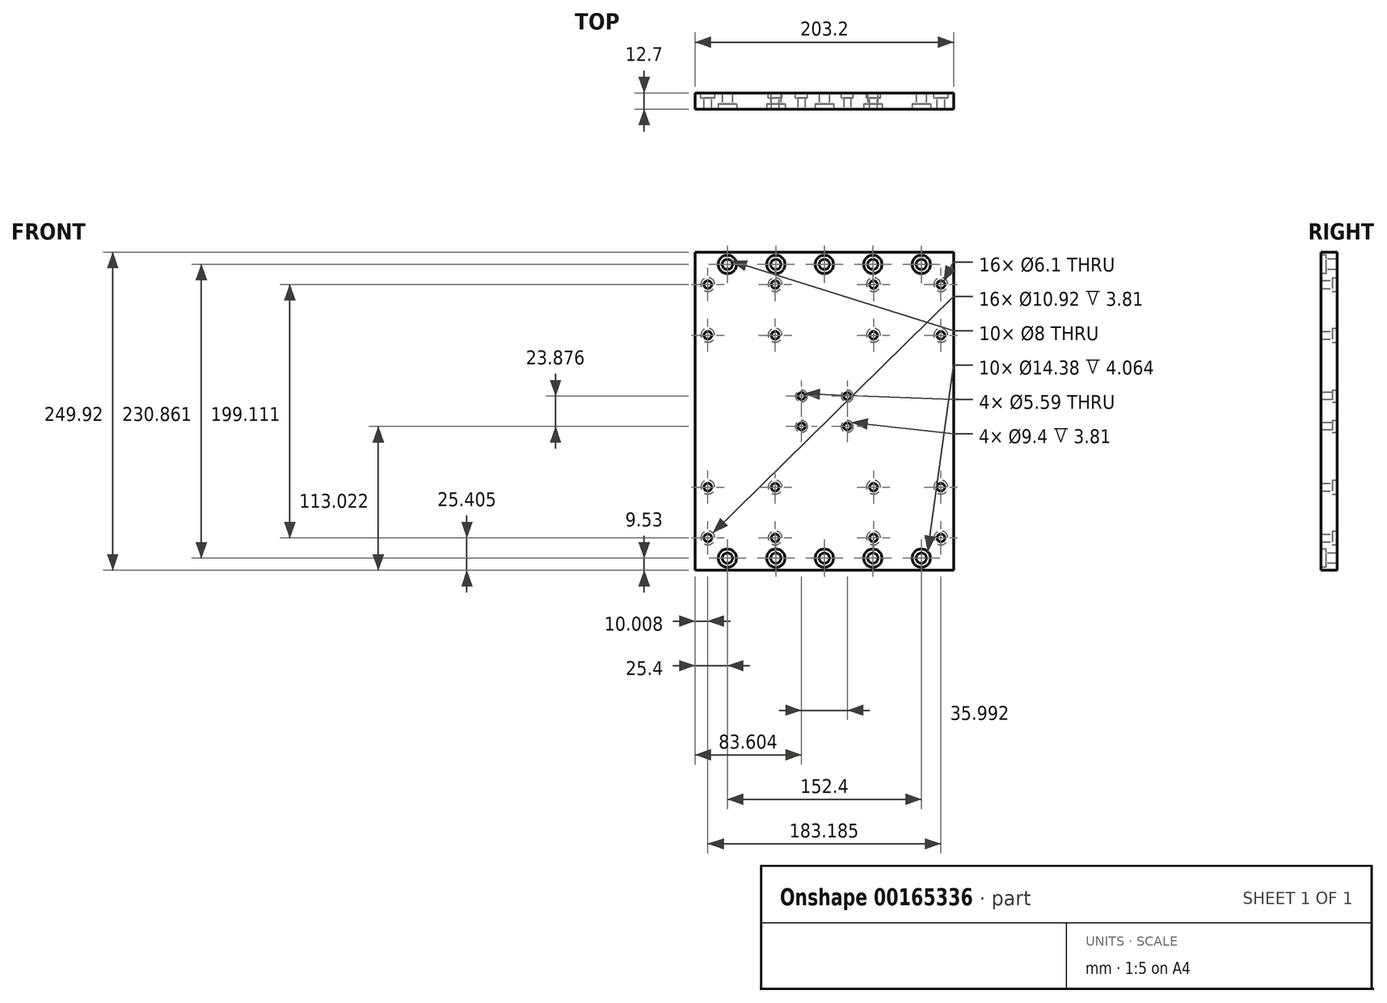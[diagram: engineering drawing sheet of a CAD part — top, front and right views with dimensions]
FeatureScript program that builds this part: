
annotation { "Feature Type Name" : "Feature", "Feature Type Description" : "" }
export const myFeature = defineFeature(function(context is Context, id is Id, definition is map)
    precondition{}
    {
        {
            var Q0;
            Q0=qCreatedBy(makeId("Front.planeOp"),FACE);
            var sketch = newSketch(context, id + "F0", { "sketchPlane" : qUnion([Q0])});
            skLineSegment(sketch, "E0.rect.bottom", {"start": v(101.6, 124.96) * mm, "end": v(-101.6, 124.96) * mm});
            skLineSegment(sketch, "E0.rect.top", {"start": v(101.6, -124.96) * mm, "end": v(-101.6, -124.96) * mm});
            skLineSegment(sketch, "E0.rect.left", {"start": v(101.6, 124.96) * mm, "end": v(101.6, -124.96) * mm});
            skLineSegment(sketch, "E0.rect.right", {"start": v(-101.6, 124.96) * mm, "end": v(-101.6, -124.96) * mm});
            skPoint(sketch, "E0.rect.middle", {"position": v(0, 0) * mm});
            skLineSegment(sketch, "E1", {"start": v(-101.6, 99.56) * mm, "end": v(101.6, 99.56) * mm, "construction": true});
            skLineSegment(sketch, "E2", {"start": v(-91.6, 124.96) * mm, "end": v(-91.6, -124.96) * mm, "construction": true});
            skLineSegment(sketch, "E3", {"start": v(-38.63, 124.96) * mm, "end": v(-38.63, -124.96) * mm, "construction": true});
            skLineSegment(sketch, "E4", {"start": v(38.63, 124.96) * mm, "end": v(38.63, -124.96) * mm, "construction": true});
            skLineSegment(sketch, "E5", {"start": v(91.6, 124.96) * mm, "end": v(91.6, -124.96) * mm, "construction": true});
            skLineSegment(sketch, "E6", {"start": v(-101.6, 59.68) * mm, "end": v(101.6, 59.68) * mm, "construction": true});
            skLineSegment(sketch, "E7", {"start": v(-101.6, -99.56) * mm, "end": v(101.6, -99.56) * mm, "construction": true});
            skLineSegment(sketch, "E8", {"start": v(-101.6, -59.68) * mm, "end": v(101.6, -59.68) * mm, "construction": true});
            skCircle(sketch, "E9", {"center": v(-91.6, 99.56) * mm, "radius": 3.05 * mm});
            skCircle(sketch, "E10", {"center": v(-38.63, 99.56) * mm, "radius": 3.05 * mm});
            skCircle(sketch, "E11", {"center": v(38.63, 99.56) * mm, "radius": 3.05 * mm});
            skCircle(sketch, "E12", {"center": v(91.6, 99.56) * mm, "radius": 3.05 * mm});
            skCircle(sketch, "E13", {"center": v(91.6, 59.68) * mm, "radius": 3.05 * mm});
            skCircle(sketch, "E14", {"center": v(-38.63, 59.68) * mm, "radius": 3.05 * mm});
            skCircle(sketch, "E15", {"center": v(38.63, 59.68) * mm, "radius": 3.05 * mm});
            skCircle(sketch, "E16", {"center": v(38.63, -59.68) * mm, "radius": 3.05 * mm});
            skCircle(sketch, "E17", {"center": v(91.6, -59.68) * mm, "radius": 3.05 * mm});
            skCircle(sketch, "E18", {"center": v(91.6, -99.56) * mm, "radius": 3.05 * mm});
            skCircle(sketch, "E19", {"center": v(38.63, -99.56) * mm, "radius": 3.05 * mm});
            skCircle(sketch, "E20", {"center": v(-38.63, -99.56) * mm, "radius": 3.05 * mm});
            skCircle(sketch, "E21", {"center": v(-38.63, -59.68) * mm, "radius": 3.05 * mm});
            skCircle(sketch, "E22", {"center": v(-91.6, -59.68) * mm, "radius": 3.05 * mm});
            skCircle(sketch, "E23", {"center": v(-91.6, -99.56) * mm, "radius": 3.05 * mm});
            skCircle(sketch, "E24", {"center": v(-91.6, 59.68) * mm, "radius": 3.05 * mm});
            skSolve(sketch);
        }
        {
            var Q0;
            Q0=qSketchRegion(id+"F0",true);
            extrude(context, id + "F1", {"entities" : qUnion([Q0]), "depth" : 12.7 * mm});
        }
        {
            var Q0;
            Q0=makeQuery(id+"F1.opExtrude","CAP_FACE",FACE,{"disambiguationData":[OSD([sQuery(id+"F0.wireOp",EDGE,"E0.rect.bottom"),sQuery(id+"F0.wireOp",EDGE,"E0.rect.top"),sQuery(id+"F0.wireOp",EDGE,"E0.rect.left"),sQuery(id+"F0.wireOp",EDGE,"E0.rect.right"),sQuery(id+"F0.wireOp",EDGE,"E9"),sQuery(id+"F0.wireOp",EDGE,"E10"),sQuery(id+"F0.wireOp",EDGE,"E11"),sQuery(id+"F0.wireOp",EDGE,"E12"),sQuery(id+"F0.wireOp",EDGE,"E13"),sQuery(id+"F0.wireOp",EDGE,"E14"),sQuery(id+"F0.wireOp",EDGE,"E15"),sQuery(id+"F0.wireOp",EDGE,"E16"),sQuery(id+"F0.wireOp",EDGE,"E17"),sQuery(id+"F0.wireOp",EDGE,"E18"),sQuery(id+"F0.wireOp",EDGE,"E19"),sQuery(id+"F0.wireOp",EDGE,"E20"),sQuery(id+"F0.wireOp",EDGE,"E21"),sQuery(id+"F0.wireOp",EDGE,"E22"),sQuery(id+"F0.wireOp",EDGE,"E23"),sQuery(id+"F0.wireOp",EDGE,"E24")])],"isStart":false});
            var sketch = newSketch(context, id + "F2", { "sketchPlane" : qUnion([Q0])});
            skPoint(sketch, "E25.rect.middle", {"position": v(0, 0) * mm});
            skLineSegment(sketch, "E26.rect.bottom", {"start": v(18, -11.94) * mm, "end": v(-18, -11.94) * mm, "construction": true});
            skLineSegment(sketch, "E26.rect.top", {"start": v(18, 11.94) * mm, "end": v(-18, 11.94) * mm, "construction": true});
            skLineSegment(sketch, "E26.rect.left", {"start": v(18, -11.94) * mm, "end": v(18, 11.94) * mm, "construction": true});
            skLineSegment(sketch, "E26.rect.right", {"start": v(-18, -11.94) * mm, "end": v(-18, 11.94) * mm, "construction": true});
            skCircle(sketch, "E27", {"center": v(-18, 11.94) * mm, "radius": 2.8 * mm});
            skCircle(sketch, "E28", {"center": v(18, 11.94) * mm, "radius": 2.8 * mm});
            skCircle(sketch, "E29", {"center": v(18, -11.94) * mm, "radius": 2.8 * mm});
            skCircle(sketch, "E30", {"center": v(-18, -11.94) * mm, "radius": 2.8 * mm});
            skSolve(sketch);
        }
        {
            var Q0;
            Q0=qSketchRegion(id+"F2",true);
            extrude(context, id + "F3", {"entities" : qUnion([Q0]), "operationType" : NewBodyOperationType.REMOVE, "endBound" : BoundingType.THROUGH_ALL, "oppositeDirection" : true, "depth" : 25.4 * mm});
        }
        {
            var Q0;
            Q0=makeQuery(id+"F1.opExtrude","CAP_FACE",FACE,{"disambiguationData":[OSD([sQuery(id+"F0.wireOp",EDGE,"E0.rect.bottom"),sQuery(id+"F0.wireOp",EDGE,"E0.rect.top"),sQuery(id+"F0.wireOp",EDGE,"E0.rect.left"),sQuery(id+"F0.wireOp",EDGE,"E0.rect.right"),sQuery(id+"F0.wireOp",EDGE,"E9"),sQuery(id+"F0.wireOp",EDGE,"E10"),sQuery(id+"F0.wireOp",EDGE,"E11"),sQuery(id+"F0.wireOp",EDGE,"E12"),sQuery(id+"F0.wireOp",EDGE,"E13"),sQuery(id+"F0.wireOp",EDGE,"E14"),sQuery(id+"F0.wireOp",EDGE,"E15"),sQuery(id+"F0.wireOp",EDGE,"E16"),sQuery(id+"F0.wireOp",EDGE,"E17"),sQuery(id+"F0.wireOp",EDGE,"E18"),sQuery(id+"F0.wireOp",EDGE,"E19"),sQuery(id+"F0.wireOp",EDGE,"E20"),sQuery(id+"F0.wireOp",EDGE,"E21"),sQuery(id+"F0.wireOp",EDGE,"E22"),sQuery(id+"F0.wireOp",EDGE,"E23"),sQuery(id+"F0.wireOp",EDGE,"E24")])],"isStart":false});
            var sketch = newSketch(context, id + "F4", { "sketchPlane" : qUnion([Q0])});
            skLineSegment(sketch, "E31", {"start": v(-101.6, -115.43) * mm, "end": v(101.6, -115.43) * mm, "construction": true});
            skLineSegment(sketch, "E32", {"start": v(-101.6, 115.43) * mm, "end": v(101.6, 115.43) * mm, "construction": true});
            skLineSegment(sketch, "E33", {"start": v(-76.2, 124.96) * mm, "end": v(-76.2, -124.96) * mm, "construction": true});
            skLineSegment(sketch, "E34", {"start": v(-38.1, 124.96) * mm, "end": v(-38.1, -124.96) * mm, "construction": true});
            skLineSegment(sketch, "E35", {"start": v(-38.1, -124.96) * mm, "end": v(-35.75, -125.26) * mm, "construction": true});
            skLineSegment(sketch, "E36", {"start": v(0, 124.96) * mm, "end": v(0, -124.96) * mm, "construction": true});
            skLineSegment(sketch, "E37", {"start": v(38.1, 124.96) * mm, "end": v(38.1, -124.96) * mm, "construction": true});
            skLineSegment(sketch, "E38", {"start": v(38.1, -124.96) * mm, "end": v(36.15, -126.04) * mm, "construction": true});
            skLineSegment(sketch, "E39", {"start": v(76.2, 124.96) * mm, "end": v(76.2, -124.96) * mm, "construction": true});
            skCircle(sketch, "E40", {"center": v(-76.2, 115.43) * mm, "radius": 4 * mm});
            skCircle(sketch, "E41", {"center": v(-38.1, 115.43) * mm, "radius": 4 * mm});
            skCircle(sketch, "E42", {"center": v(0, 115.43) * mm, "radius": 4 * mm});
            skCircle(sketch, "E43", {"center": v(38.1, 115.43) * mm, "radius": 4 * mm});
            skCircle(sketch, "E44", {"center": v(76.2, 115.43) * mm, "radius": 4 * mm});
            skCircle(sketch, "E45", {"center": v(-76.2, -115.43) * mm, "radius": 4 * mm});
            skCircle(sketch, "E46", {"center": v(-38.1, -115.43) * mm, "radius": 4 * mm});
            skCircle(sketch, "E47", {"center": v(0, -115.43) * mm, "radius": 4 * mm});
            skCircle(sketch, "E48", {"center": v(38.1, -115.43) * mm, "radius": 4 * mm});
            skCircle(sketch, "E49", {"center": v(76.2, -115.43) * mm, "radius": 4 * mm});
            skSolve(sketch);
        }
        {
            var Q0;
            Q0=qSketchRegion(id+"F4",true);
            extrude(context, id + "F5", {"entities" : qUnion([Q0]), "operationType" : NewBodyOperationType.REMOVE, "endBound" : BoundingType.THROUGH_ALL, "oppositeDirection" : true, "depth" : 25.4 * mm});
        }
        {
            var Q0;
            Q0=qSketchRegion(id+"F2",true);
            extrude(context, id + "F6", {"entities" : qUnion([Q0]), "operationType" : NewBodyOperationType.REMOVE, "endBound" : BoundingType.THROUGH_ALL, "oppositeDirection" : true, "depth" : 25.4 * mm});
        }
        {
            var Q0;
            Q0=makeQuery(id+"F1.opExtrude","CAP_FACE",FACE,{"disambiguationData":[OSD([sQuery(id+"F0.wireOp",EDGE,"E0.rect.bottom"),sQuery(id+"F0.wireOp",EDGE,"E0.rect.top"),sQuery(id+"F0.wireOp",EDGE,"E0.rect.left"),sQuery(id+"F0.wireOp",EDGE,"E0.rect.right"),sQuery(id+"F0.wireOp",EDGE,"E9"),sQuery(id+"F0.wireOp",EDGE,"E10"),sQuery(id+"F0.wireOp",EDGE,"E11"),sQuery(id+"F0.wireOp",EDGE,"E12"),sQuery(id+"F0.wireOp",EDGE,"E13"),sQuery(id+"F0.wireOp",EDGE,"E14"),sQuery(id+"F0.wireOp",EDGE,"E15"),sQuery(id+"F0.wireOp",EDGE,"E16"),sQuery(id+"F0.wireOp",EDGE,"E17"),sQuery(id+"F0.wireOp",EDGE,"E18"),sQuery(id+"F0.wireOp",EDGE,"E19"),sQuery(id+"F0.wireOp",EDGE,"E20"),sQuery(id+"F0.wireOp",EDGE,"E21"),sQuery(id+"F0.wireOp",EDGE,"E22"),sQuery(id+"F0.wireOp",EDGE,"E23"),sQuery(id+"F0.wireOp",EDGE,"E24")])],"isStart":false});
            var sketch = newSketch(context, id + "F7", { "sketchPlane" : qUnion([Q0])});
            skCircle(sketch, "E50", {"center": v(0, -115.43) * mm, "radius": 7.19 * mm});
            skCircle(sketch, "E51", {"center": v(0, 115.43) * mm, "radius": 7.19 * mm});
            skCircle(sketch, "E52", {"center": v(-38.1, -115.43) * mm, "radius": 7.19 * mm});
            skCircle(sketch, "E53", {"center": v(-76.2, -115.43) * mm, "radius": 7.19 * mm});
            skCircle(sketch, "E54", {"center": v(38.1, -115.43) * mm, "radius": 7.19 * mm});
            skCircle(sketch, "E55", {"center": v(76.2, -115.43) * mm, "radius": 7.19 * mm});
            skCircle(sketch, "E56", {"center": v(-76.2, 115.43) * mm, "radius": 7.19 * mm});
            skCircle(sketch, "E57", {"center": v(-38.1, 115.43) * mm, "radius": 7.19 * mm});
            skCircle(sketch, "E58", {"center": v(38.1, 115.43) * mm, "radius": 7.19 * mm});
            skCircle(sketch, "E59", {"center": v(76.2, 115.43) * mm, "radius": 7.19 * mm});
            skSolve(sketch);
        }
        {
            var Q0;
            Q0=qSketchRegion(id+"F7",true);
            extrude(context, id + "F8", {"entities" : qUnion([Q0]), "operationType" : NewBodyOperationType.REMOVE, "oppositeDirection" : true, "depth" : 4.06 * mm});
        }
        {
            var Q0;
            Q0=makeQuery(id+"F1.opExtrude","CAP_FACE",FACE,{"disambiguationData":[OSD([sQuery(id+"F0.wireOp",EDGE,"E0.rect.bottom"),sQuery(id+"F0.wireOp",EDGE,"E0.rect.top"),sQuery(id+"F0.wireOp",EDGE,"E0.rect.left"),sQuery(id+"F0.wireOp",EDGE,"E0.rect.right"),sQuery(id+"F0.wireOp",EDGE,"E9"),sQuery(id+"F0.wireOp",EDGE,"E10"),sQuery(id+"F0.wireOp",EDGE,"E11"),sQuery(id+"F0.wireOp",EDGE,"E12"),sQuery(id+"F0.wireOp",EDGE,"E13"),sQuery(id+"F0.wireOp",EDGE,"E14"),sQuery(id+"F0.wireOp",EDGE,"E15"),sQuery(id+"F0.wireOp",EDGE,"E16"),sQuery(id+"F0.wireOp",EDGE,"E17"),sQuery(id+"F0.wireOp",EDGE,"E18"),sQuery(id+"F0.wireOp",EDGE,"E19"),sQuery(id+"F0.wireOp",EDGE,"E20"),sQuery(id+"F0.wireOp",EDGE,"E21"),sQuery(id+"F0.wireOp",EDGE,"E22"),sQuery(id+"F0.wireOp",EDGE,"E23"),sQuery(id+"F0.wireOp",EDGE,"E24")])],"isStart":true});
            var sketch = newSketch(context, id + "F9", { "sketchPlane" : qUnion([Q0])});
            skCircle(sketch, "E60", {"center": v(-91.6, 99.56) * mm, "radius": 5.46 * mm});
            skCircle(sketch, "E61", {"center": v(-38.63, 99.56) * mm, "radius": 5.46 * mm});
            skCircle(sketch, "E62", {"center": v(38.63, 99.56) * mm, "radius": 5.46 * mm});
            skCircle(sketch, "E63", {"center": v(91.6, 99.56) * mm, "radius": 5.46 * mm});
            skCircle(sketch, "E64", {"center": v(-91.6, 59.68) * mm, "radius": 5.46 * mm});
            skCircle(sketch, "E65", {"center": v(-38.63, 59.68) * mm, "radius": 5.46 * mm});
            skCircle(sketch, "E66", {"center": v(38.63, 59.68) * mm, "radius": 5.46 * mm});
            skCircle(sketch, "E67", {"center": v(91.6, 59.68) * mm, "radius": 5.46 * mm});
            skCircle(sketch, "E68", {"center": v(-91.6, -59.68) * mm, "radius": 5.46 * mm});
            skCircle(sketch, "E69", {"center": v(-38.63, -59.68) * mm, "radius": 5.46 * mm});
            skCircle(sketch, "E70", {"center": v(38.63, -59.68) * mm, "radius": 5.46 * mm});
            skCircle(sketch, "E71", {"center": v(91.6, -59.68) * mm, "radius": 5.46 * mm});
            skCircle(sketch, "E72", {"center": v(91.6, -99.56) * mm, "radius": 5.46 * mm});
            skCircle(sketch, "E73", {"center": v(38.63, -99.56) * mm, "radius": 5.46 * mm});
            skCircle(sketch, "E74", {"center": v(-38.63, -99.56) * mm, "radius": 5.46 * mm});
            skCircle(sketch, "E75", {"center": v(-91.6, -99.56) * mm, "radius": 5.46 * mm});
            skCircle(sketch, "E76", {"center": v(-18, 11.94) * mm, "radius": 4.7 * mm});
            skCircle(sketch, "E77", {"center": v(18, 11.94) * mm, "radius": 4.7 * mm});
            skCircle(sketch, "E78", {"center": v(18, -11.94) * mm, "radius": 4.7 * mm});
            skCircle(sketch, "E79", {"center": v(-18, -11.94) * mm, "radius": 4.7 * mm});
            skSolve(sketch);
        }
        {
            var Q0;
            Q0=qSketchRegion(id+"F9",true);
            extrude(context, id + "F10", {"entities" : qUnion([Q0]), "operationType" : NewBodyOperationType.REMOVE, "oppositeDirection" : true, "depth" : 3.8 * mm});
        }
    });
